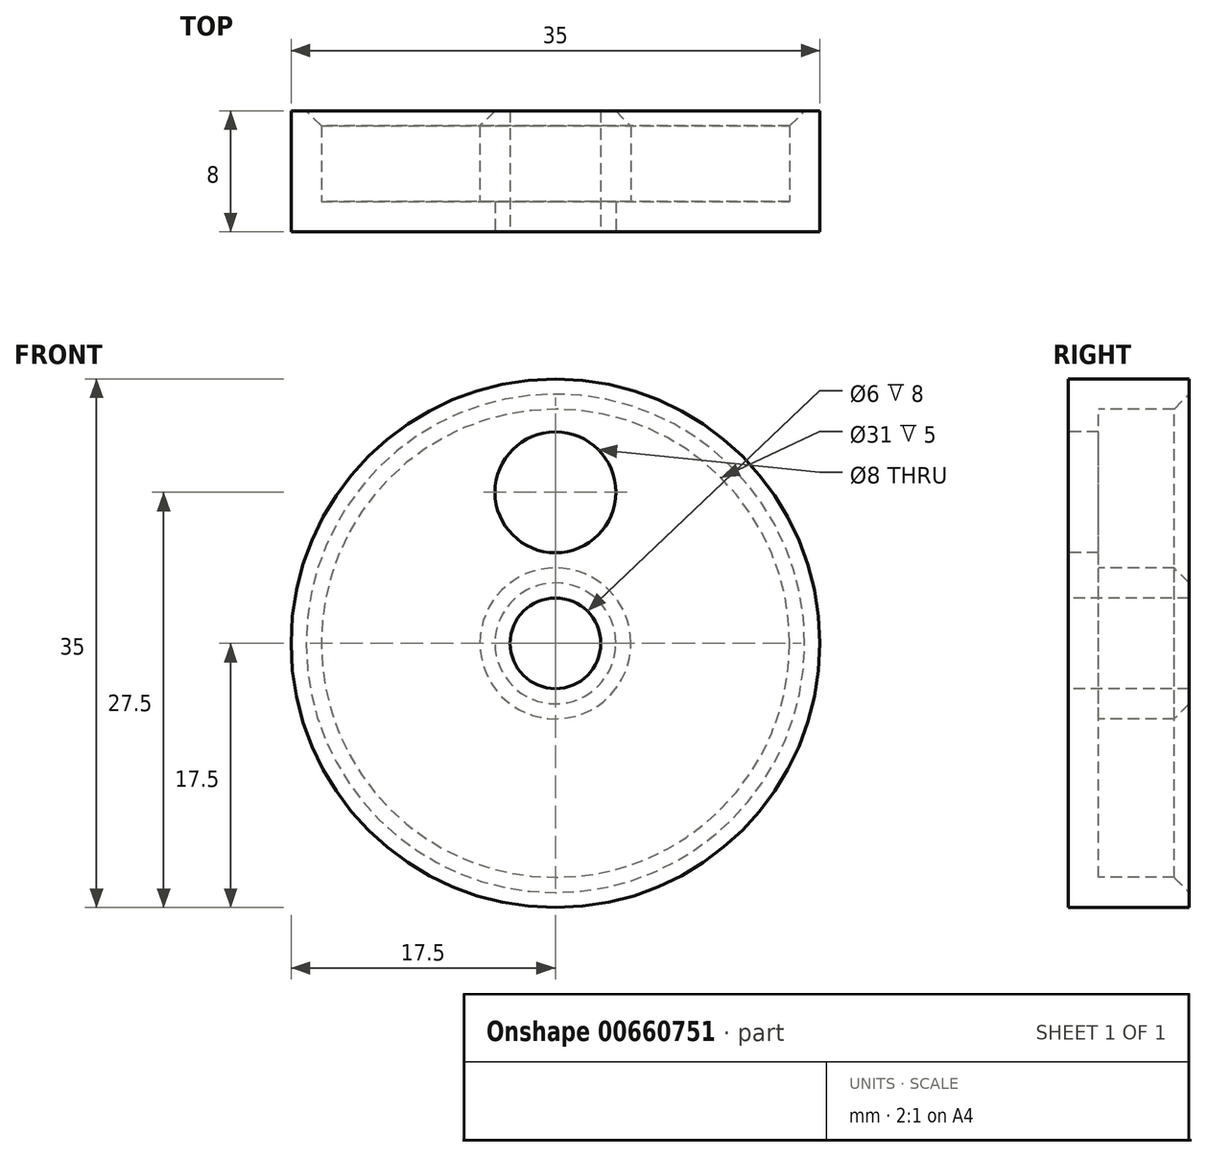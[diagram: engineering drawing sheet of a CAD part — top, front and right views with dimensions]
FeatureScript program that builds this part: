
annotation { "Feature Type Name" : "Feature", "Feature Type Description" : "" }
export const myFeature = defineFeature(function(context is Context, id is Id, definition is map)
    precondition{}
    {
        {
            var Q0;
            Q0=qCreatedBy(makeId("Right.planeOp"),FACE);
            var sketch = newSketch(context, id + "F0", { "sketchPlane" : qUnion([Q0])});
            skLineSegment(sketch, "E0.bottom", {"start": v(0, 0) * mm, "end": v(8, 0) * mm});
            skLineSegment(sketch, "E0.top", {"start": v(0, 17.5) * mm, "end": v(8, 17.5) * mm});
            skLineSegment(sketch, "E0.left", {"start": v(0, 0) * mm, "end": v(0, 17.5) * mm});
            skLineSegment(sketch, "E0.right", {"start": v(8, 0) * mm, "end": v(8, 17.5) * mm});
            skSolve(sketch);
        }
        {
            var Q0;
            Q0 = qSketchRegion(id + "F0", true);
            var Q1;
            Q1=sQuery(id+"F0.wireOp",EDGE,"E0.bottom");
            revolve(context, id + "F1", {"entities" : qUnion([Q0]), "axis" : qUnion([Q1]), "revolveType" : RevolveType.FULL});
        }
        {
            var Q0;
            Q0=qCreatedBy(makeId("Front.planeOp"),FACE);
            var sketch = newSketch(context, id + "F2", { "sketchPlane" : qUnion([Q0])});
            skPoint(sketch, "E1", {"position": v(0, 0) * mm});
            skSolve(sketch);
        }
        {
            var Q0;
            Q0=sQuery(id+"F2.wireOp",VERTEX,"E1");
            var Q1;
            Q1=makeQuery(id+"F1.opRevolve","SWEPT_BODY",BODY,{"disambiguationData":[OSD([sQuery(id+"F0.wireOp",EDGE,"E0.bottom"),sQuery(id+"F0.wireOp",EDGE,"E0.top"),sQuery(id+"F0.wireOp",EDGE,"E0.left"),sQuery(id+"F0.wireOp",EDGE,"E0.right")])]});
            hole(context, id + "F3", {"style" : HoleStyle.SIMPLE, "endStyle" : HoleEndStyle.THROUGH, "holeDiameter" : 6 * mm, "majorDiameter" : 5 * mm, "isTappedThrough" : true, "tappedDepth" : 12 * mm, "tapClearance" : 3, "locations" : qUnion([Q0]), "scope" : qUnion([Q1])});
        }
        {
            var Q0;
            Q0=makeQuery(id+"F1.opRevolve","SWEPT_FACE",FACE,{"disambiguationData":[OSD([sQuery(id+"F0.wireOp",EDGE,"E0.right")])]});
            shell(context, id + "F4", {"entities" : qUnion([Q0]), "thickness" : 2 * mm});
        }
        {
            var Q0;
            Q0=makeQuery(id+"F1.opRevolve","SWEPT_FACE",FACE,{"disambiguationData":[OSD([sQuery(id+"F0.wireOp",EDGE,"E0.left")])]});
            var sketch = newSketch(context, id + "F5", { "sketchPlane" : qUnion([Q0])});
            skPoint(sketch, "E2", {"position": v(0, 0) * mm});
            skPoint(sketch, "E3", {"position": v(0, 10) * mm});
            skSolve(sketch);
        }
        {
            var Q0;
            Q0=sQuery(id+"F5.wireOp",VERTEX,"E3");
            var Q1;
            Q1=makeQuery(id+"F1.opRevolve","SWEPT_BODY",BODY,{"disambiguationData":[OSD([sQuery(id+"F0.wireOp",EDGE,"E0.bottom"),sQuery(id+"F0.wireOp",EDGE,"E0.top"),sQuery(id+"F0.wireOp",EDGE,"E0.left"),sQuery(id+"F0.wireOp",EDGE,"E0.right")])]});
            hole(context, id + "F6", {"style" : HoleStyle.SIMPLE, "endStyle" : HoleEndStyle.THROUGH, "holeDiameter" : 8 * mm, "majorDiameter" : 5 * mm, "isTappedThrough" : true, "tappedDepth" : 12 * mm, "tapClearance" : 3, "locations" : qUnion([Q0]), "scope" : qUnion([Q1])});
        }
        {
            var Q0;
            Q0=makeQuery(id+"F4.opShell","OFFSET_EDGE",EDGE,{"disambiguationData":[OSD([sQuery(id+"F0.wireOp",EDGE,"E0.right"),sQuery(id+"F3.hole-0.sketch.wireOp",EDGE,"core_line_2")])]});
            chamfer(context, id + "F7", {"entities" : qUnion([Q0]), "width" : 1 * mm, "tangentPropagation" : true});
        }
    });
